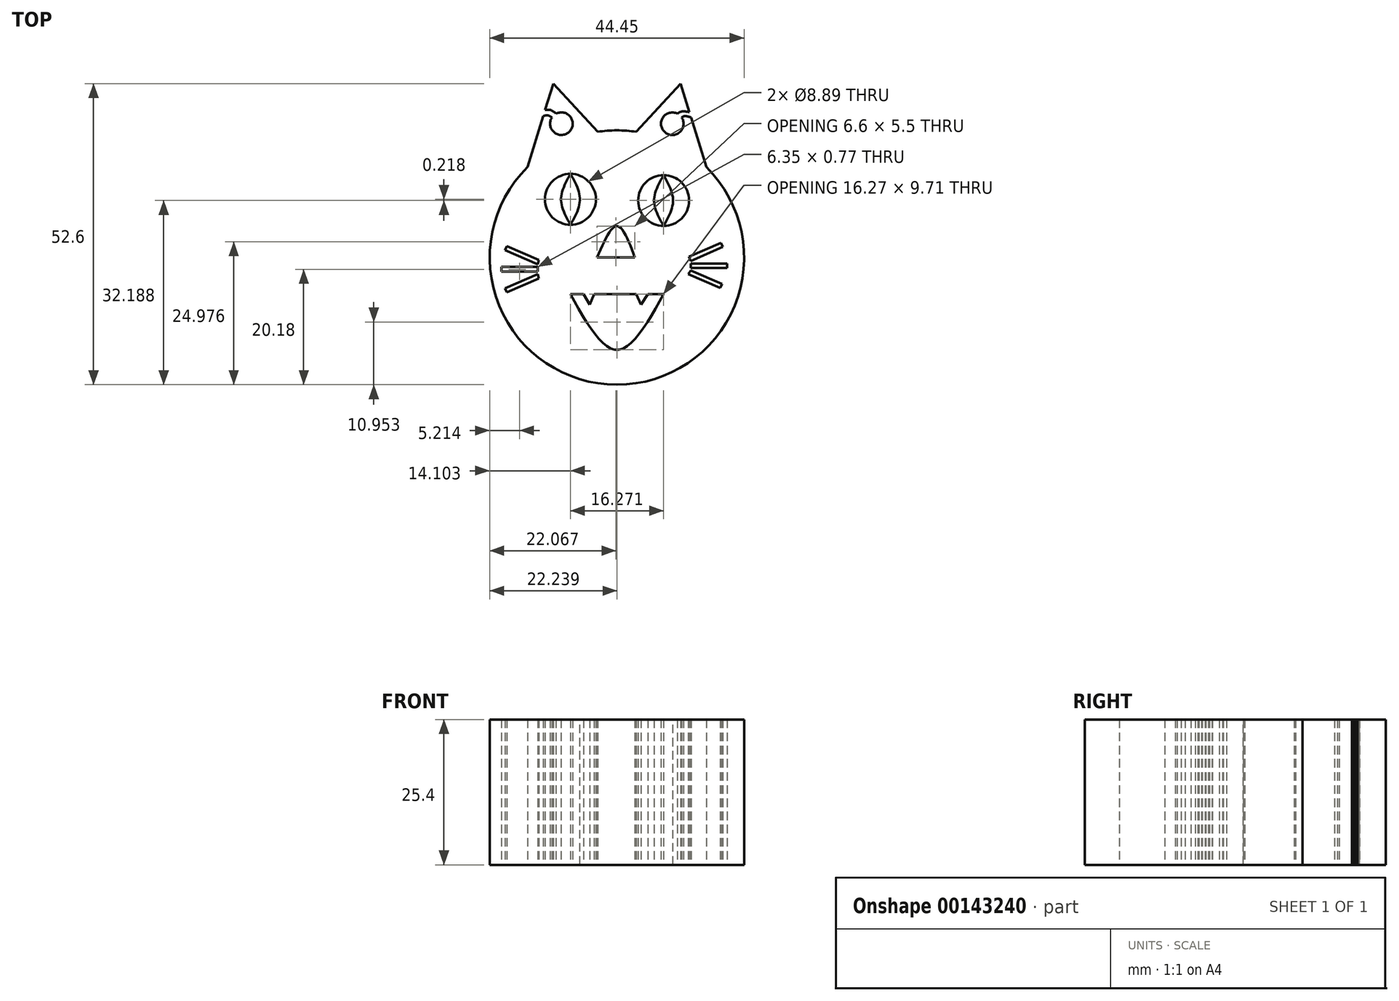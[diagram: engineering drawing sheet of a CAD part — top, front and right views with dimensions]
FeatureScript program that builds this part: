
annotation { "Feature Type Name" : "Feature", "Feature Type Description" : "" }
export const myFeature = defineFeature(function(context is Context, id is Id, definition is map)
    precondition{}
    {
        {
            var Q0;
            Q0=qCreatedBy(makeId("Top.planeOp"),FACE);
            var sketch = newSketch(context, id + "F0", { "sketchPlane" : qUnion([Q0])});
            skCircle(sketch, "E0", {"center": v(0.3, -6.58) * mm, "radius": 22.23 * mm});
            skLineSegment(sketch, "E1", {"start": v(-15.32, 9.23) * mm, "end": v(-10.82, 23.8) * mm});
            skLineSegment(sketch, "E2", {"start": v(-10.82, 23.8) * mm, "end": v(-3.08, 15.38) * mm});
            skLineSegment(sketch, "E3", {"start": v(15.92, 9.23) * mm, "end": v(11.43, 23.8) * mm});
            skLineSegment(sketch, "E4", {"start": v(11.43, 23.8) * mm, "end": v(3.69, 15.38) * mm});
            skCircle(sketch, "E5", {"center": v(-7.82, 3.6) * mm, "radius": 4.45 * mm});
            skCircle(sketch, "E6", {"center": v(8.45, 3.38) * mm, "radius": 4.45 * mm});
            skLineSegment(sketch, "E7", {"start": v(-3.15, -6.58) * mm, "end": v(3.45, -6.58) * mm});
            skFitSpline(sketch, "E8", {"points": [v(3.45, -6.58) * mm, v(0.3, -1.08) * mm, v(-3.15, -6.58) * mm], "startDerivative": vector(-6.19, 16.53) * mm, "endDerivative": vector(-7, -16.46) * mm});
            skLineSegment(sketch, "E9", {"start": v(-7.82, -13) * mm, "end": v(-5.52, -13) * mm});
            skFitSpline(sketch, "E10", {"points": [v(8.45, -13) * mm, v(0.3, -22.71) * mm, v(-7.82, -13) * mm], "startDerivative": vector(-16.3, -29.14) * mm, "endDerivative": vector(-16.24, 29.15) * mm});
            skLineSegment(sketch, "E11", {"start": v(-5.52, -13) * mm, "end": v(-4.47, -14.82) * mm});
            skLineSegment(sketch, "E12", {"start": v(-4.47, -14.82) * mm, "end": v(-3.69, -13) * mm});
            skLineSegment(sketch, "E13", {"start": v(3.69, -13) * mm, "end": v(4.51, -14.82) * mm});
            skLineSegment(sketch, "E14", {"start": v(4.51, -14.82) * mm, "end": v(5.7, -13) * mm});
            skLineSegment(sketch, "E15.trimOffspring", {"start": v(-3.69, -13) * mm, "end": v(3.69, -13) * mm});
            skLineSegment(sketch, "E16.trimOffspring", {"start": v(5.7, -13) * mm, "end": v(8.45, -13) * mm});
            skFitSpline(sketch, "E17", {"points": [v(-7.82, 8.04) * mm, v(-9.46, 3.6) * mm, v(-7.82, -0.85) * mm], "startDerivative": vector(-4.93, -8.9) * mm, "endDerivative": vector(4.93, -8.89) * mm});
            skFitSpline(sketch, "E18", {"points": [v(-7.82, 8.04) * mm, v(-6.15, 3.6) * mm, v(-7.82, -0.85) * mm], "startDerivative": vector(4.99, -8.9) * mm, "endDerivative": vector(-4.99, -8.9) * mm});
            skFitSpline(sketch, "E19", {"points": [v(8.45, 7.82) * mm, v(6.8, 3.38) * mm, v(8.45, -1.07) * mm], "startDerivative": vector(-4.94, -8.9) * mm, "endDerivative": vector(4.94, -8.9) * mm});
            skFitSpline(sketch, "E20", {"points": [v(8.45, 7.82) * mm, v(10.1, 3.38) * mm, v(8.45, -1.07) * mm], "startDerivative": vector(4.94, -8.9) * mm, "endDerivative": vector(-4.94, -8.89) * mm});
            skCircle(sketch, "E21", {"center": v(-9.4, 16.8) * mm, "radius": 1.97 * mm});
            skCircle(sketch, "E22", {"center": v(9.98, 16.8) * mm, "radius": 1.97 * mm});
            skFitSpline(sketch, "E23", {"points": [v(-10.32, 18.55) * mm, v(-11.3, 19.2) * mm, v(-12.24, 19.2) * mm], "startDerivative": vector(-1.84, 1.54) * mm, "endDerivative": vector(-2, -0.26) * mm});
            skFitSpline(sketch, "E24", {"points": [v(-11.03, 17.9) * mm, v(-11.77, 18.27) * mm, v(-12.56, 18.15) * mm], "startDerivative": vector(-1.43, 0.96) * mm, "endDerivative": vector(-1.63, -0.48) * mm});
            skFitSpline(sketch, "E25", {"points": [v(10.87, 18.55) * mm, v(11.58, 18.92) * mm, v(12.96, 18.84) * mm], "startDerivative": vector(1.47, 1.08) * mm, "endDerivative": vector(2.65, -0.42) * mm});
            skFitSpline(sketch, "E26", {"points": [v(11.6, 17.9) * mm, v(12.12, 18.13) * mm, v(13.25, 17.9) * mm], "startDerivative": vector(1.12, 0.75) * mm, "endDerivative": vector(2.1, -0.66) * mm});
            skLineSegment(sketch, "E27.bottom", {"start": v(-13.53, -8.24) * mm, "end": v(-19.88, -8.24) * mm});
            skLineSegment(sketch, "E27.top", {"start": v(-13.53, -9.02) * mm, "end": v(-19.88, -9.02) * mm});
            skLineSegment(sketch, "E27.left", {"start": v(-13.53, -8.24) * mm, "end": v(-13.53, -9.02) * mm});
            skLineSegment(sketch, "E27.right", {"start": v(-19.88, -8.24) * mm, "end": v(-19.88, -9.02) * mm});
            skLineSegment(sketch, "E28", {"start": v(-13.54, -7.78) * mm, "end": v(-19.23, -5.3) * mm});
            skLineSegment(sketch, "E29", {"start": v(-19.23, -5.3) * mm, "end": v(-18.92, -4.6) * mm});
            skLineSegment(sketch, "E30", {"start": v(-18.92, -4.6) * mm, "end": v(-13.36, -7.03) * mm});
            skLineSegment(sketch, "E31", {"start": v(-13.36, -7.03) * mm, "end": v(-13.54, -7.78) * mm});
            skLineSegment(sketch, "E32", {"start": v(-13.53, -9.47) * mm, "end": v(-19.23, -11.95) * mm});
            skLineSegment(sketch, "E33", {"start": v(-19.23, -11.95) * mm, "end": v(-18.92, -12.65) * mm});
            skLineSegment(sketch, "E34", {"start": v(-18.92, -12.65) * mm, "end": v(-13.36, -10.23) * mm});
            skLineSegment(sketch, "E35", {"start": v(-13.36, -10.23) * mm, "end": v(-13.53, -9.47) * mm});
            skLineSegment(sketch, "E36", {"start": v(-19.88, -8.63) * mm, "end": v(-21.83, -8.63) * mm, "construction": true});
            skLineSegment(sketch, "E37.bottom", {"start": v(13.19, -7.63) * mm, "end": v(19.54, -7.63) * mm});
            skLineSegment(sketch, "E37.top", {"start": v(13.19, -8.39) * mm, "end": v(19.54, -8.39) * mm});
            skLineSegment(sketch, "E37.left", {"start": v(13.19, -7.63) * mm, "end": v(13.19, -8.39) * mm});
            skLineSegment(sketch, "E37.right", {"start": v(19.54, -7.63) * mm, "end": v(19.54, -8.39) * mm});
            skLineSegment(sketch, "E38", {"start": v(13.19, -7.17) * mm, "end": v(18.76, -4.74) * mm});
            skLineSegment(sketch, "E39", {"start": v(18.76, -4.74) * mm, "end": v(18.46, -4.04) * mm});
            skLineSegment(sketch, "E40", {"start": v(18.46, -4.04) * mm, "end": v(12.9, -6.47) * mm});
            skLineSegment(sketch, "E41", {"start": v(12.9, -6.47) * mm, "end": v(13.19, -7.17) * mm});
            skLineSegment(sketch, "E42", {"start": v(13.19, -8.84) * mm, "end": v(18.66, -11.23) * mm});
            skLineSegment(sketch, "E43", {"start": v(18.66, -11.23) * mm, "end": v(18.36, -11.92) * mm});
            skLineSegment(sketch, "E44", {"start": v(18.36, -11.92) * mm, "end": v(12.79, -9.5) * mm});
            skLineSegment(sketch, "E45", {"start": v(12.79, -9.5) * mm, "end": v(13.19, -8.84) * mm});
            skSolve(sketch);
        }
        {
            var Q0;
            {var subQ0=sQuery(id+"F0.wireOp",EDGE,"E4");Q0=makeQuery(id+"F0.imprint","IMPRINT",FACE,{"disambiguationData":[TD([[makeQuery(id+"F0.imprint","IMPRINT",EDGE,{"derivedFrom":subQ0}),1.0]])]});}
            var Q1;
            {var subQ0=sQuery(id+"F0.wireOp",EDGE,"E2");Q1=makeQuery(id+"F0.imprint","IMPRINT",FACE,{"disambiguationData":[TD([[makeQuery(id+"F0.imprint","IMPRINT",EDGE,{"derivedFrom":subQ0}),-1.0]])]});}
            var Q2;
            Q2=makeQuery(id+"F0.imprint","IMPRINT",FACE,{"disambiguationData":[TD([[makeQuery(id+"F0.imprint","IMPRINT",EDGE,{"derivedFrom":sQuery(id+"F0.wireOp",EDGE,"E7")}),-1.0]])]});
            var Q3;
            Q3=makeQuery(id+"F0.imprint","IMPRINT",FACE,{"disambiguationData":[TD([[makeQuery(id+"F0.imprint","IMPRINT",EDGE,{"derivedFrom":sQuery(id+"F0.wireOp",EDGE,"E17")}),1.0]])]});
            var Q4;
            Q4=makeQuery(id+"F0.imprint","IMPRINT",FACE,{"disambiguationData":[TD([[makeQuery(id+"F0.imprint","IMPRINT",EDGE,{"derivedFrom":sQuery(id+"F0.wireOp",EDGE,"E19")}),1.0]])]});
            extrude(context, id + "F1", {"entities" : qUnion([Q0, Q1, Q2, Q3, Q4]), "depth" : 25.4 * mm});
        }
    });
